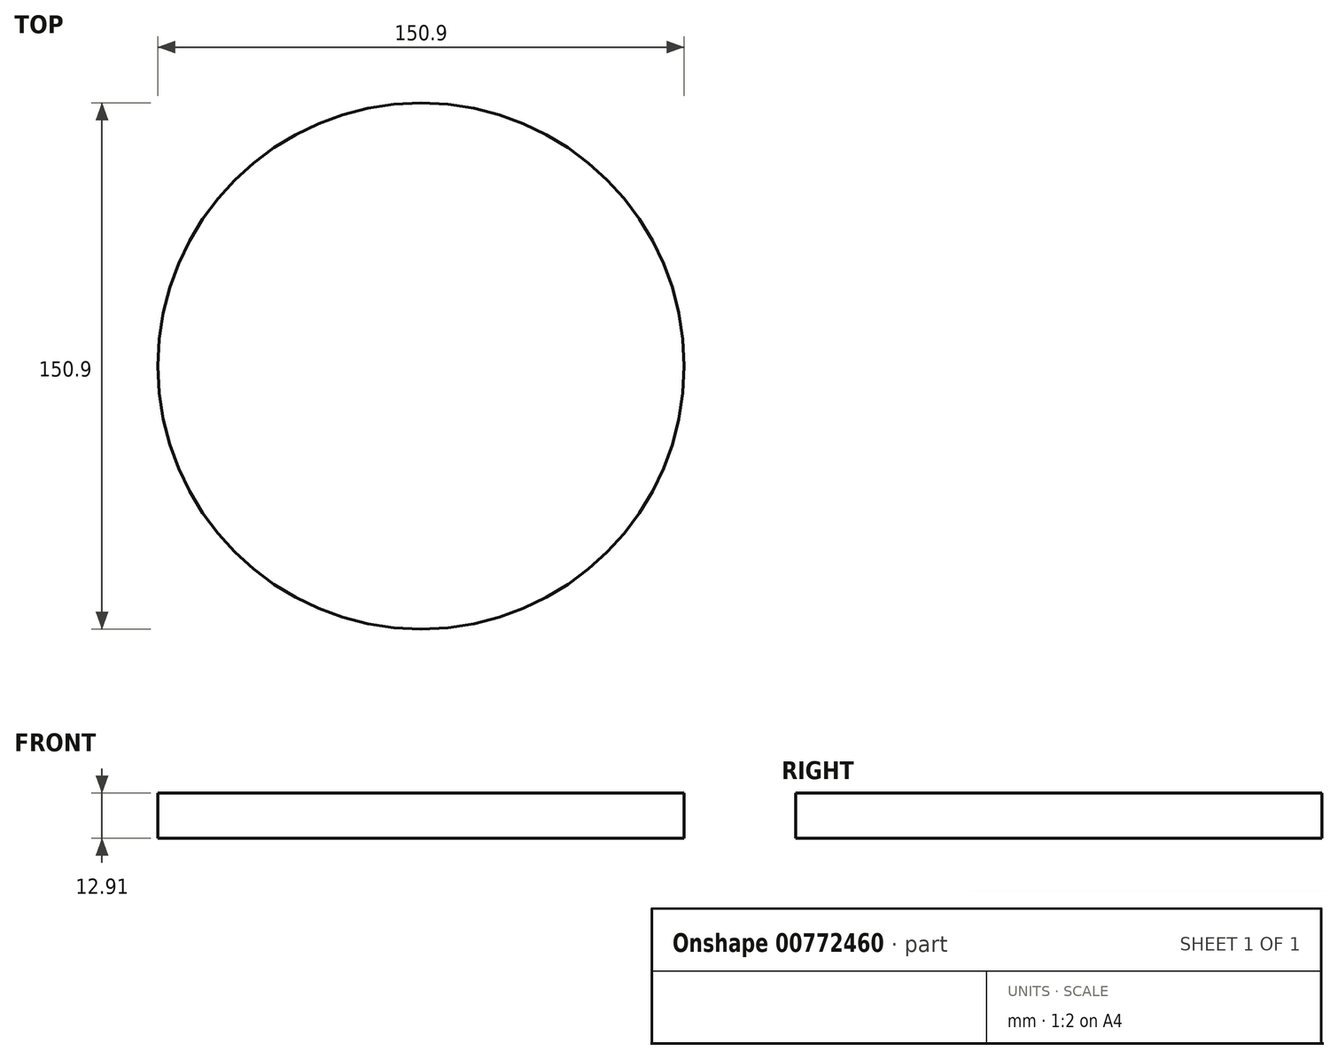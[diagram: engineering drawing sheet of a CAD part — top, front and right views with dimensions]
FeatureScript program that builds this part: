
annotation { "Feature Type Name" : "Feature", "Feature Type Description" : "" }
export const myFeature = defineFeature(function(context is Context, id is Id, definition is map)
    precondition{}
    {
        {
            var Q0;
            Q0=qCreatedBy(makeId("Top.planeOp"),FACE);
            var sketch = newSketch(context, id + "F0", { "sketchPlane" : qUnion([Q0])});
            skCircle(sketch, "E0", {"center": v(0, 0) * mm, "radius": 75.45 * mm});
            skSolve(sketch);
        }
        {
            var Q0;
            Q0=makeQuery(id+"F0.imprint","IMPRINT",FACE,{"disambiguationData":[TD([[makeQuery(id+"F0.imprint","IMPRINT",EDGE,{"derivedFrom":sQuery(id+"F0.wireOp",EDGE,"E0")}),1.0]])]});
            extrude(context, id + "F1", {"entities" : qUnion([Q0]), "depth" : 12.9 * mm, "offsetDistance" : 25 * mm});
        }
    });
